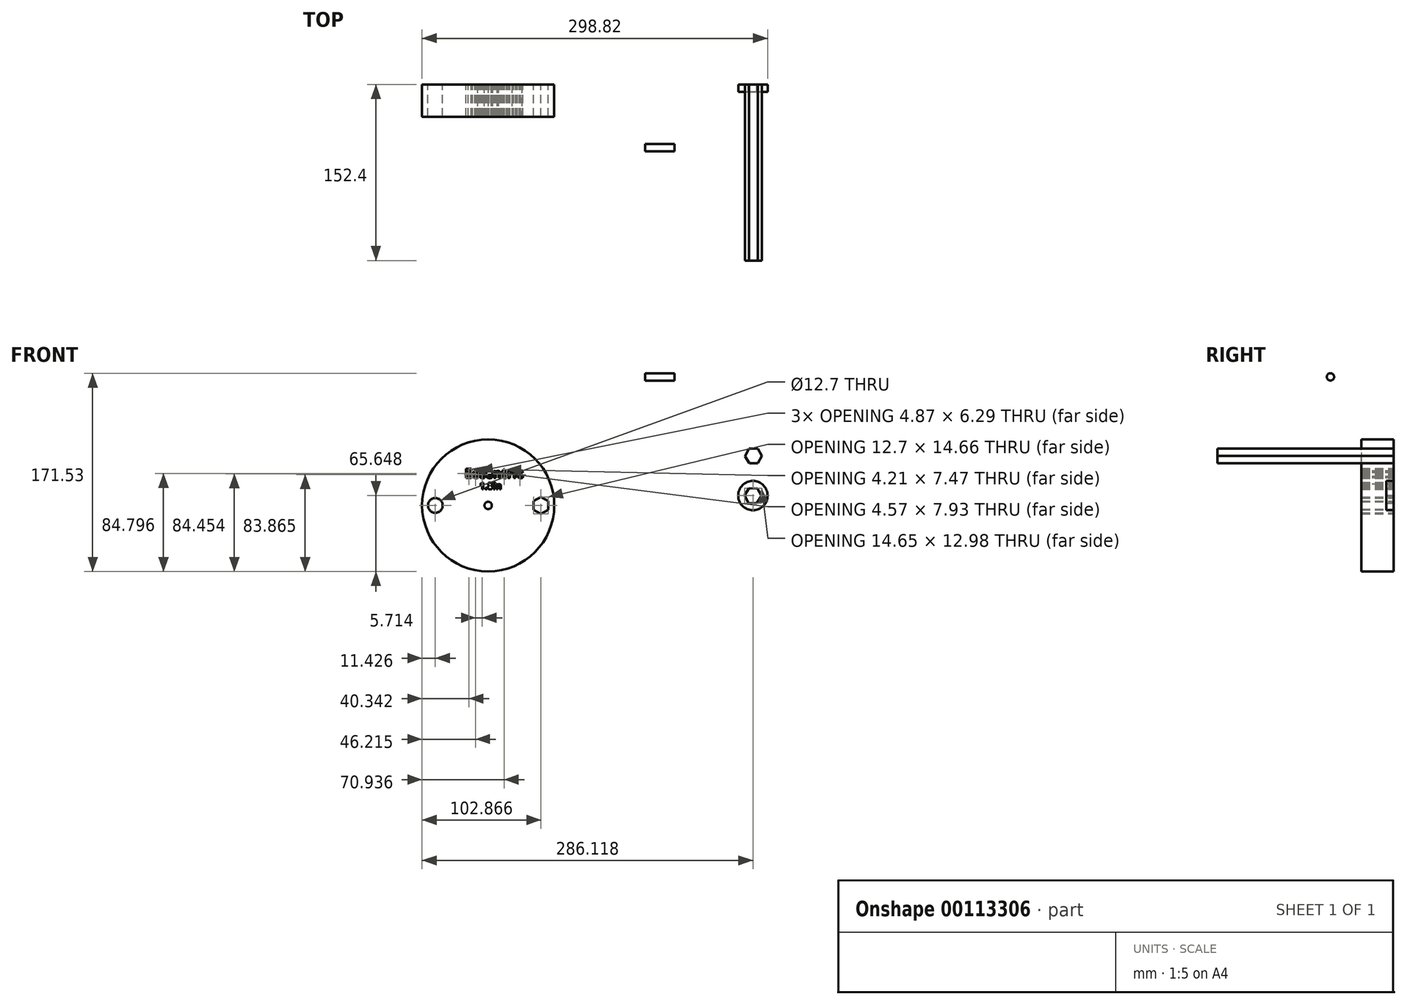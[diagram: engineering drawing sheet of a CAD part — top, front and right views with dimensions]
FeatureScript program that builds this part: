
annotation { "Feature Type Name" : "Feature", "Feature Type Description" : "" }
export const myFeature = defineFeature(function(context is Context, id is Id, definition is map)
    precondition{}
    {
        {
            var Q0;
            Q0=qCreatedBy(makeId("Front.planeOp"),FACE);
            var sketch = newSketch(context, id + "F0", { "sketchPlane" : qUnion([Q0])});
            skCircle(sketch, "E0", {"center": v(0, 0) * mm, "radius": 53.98 * mm});
            skCircle(sketch, "E1", {"center": v(0, 0) * mm, "radius": 45.72 * mm, "construction": true});
            skLineSegment(sketch, "E2", {"start": v(0, 0) * mm, "end": v(45.72, 0) * mm, "construction": true});
            skLineSegment(sketch, "E3", {"start": v(0, 0) * mm, "end": v(-22.86, 39.6) * mm, "construction": true});
            skLineSegment(sketch, "E4", {"start": v(0, 0) * mm, "end": v(-22.86, -39.6) * mm, "construction": true});
            skCircle(sketch, "E5", {"center": v(45.72, 0) * mm, "radius": 3.18 * mm});
            skCircle(sketch, "E6", {"center": v(-22.86, 39.6) * mm, "radius": 3.18 * mm});
            skCircle(sketch, "E7", {"center": v(-22.86, -39.6) * mm, "radius": 3.18 * mm});
            skCircle(sketch, "E8", {"center": v(0, 0) * mm, "radius": 3.18 * mm});
            skSolve(sketch);
        }
        {
            var Q0;
            Q0=makeQuery(id+"F0.imprint","IMPRINT",FACE,{"disambiguationData":[TD([[makeQuery(id+"F0.imprint","IMPRINT",EDGE,{"derivedFrom":sQuery(id+"F0.wireOp",EDGE,"E0")}),1.0]])]});
            extrude(context, id + "F1", {"entities" : qUnion([Q0]), "depth" : 3.17 * mm});
        }
        {
            var Q0;
            Q0=qCreatedBy(makeId("Right.planeOp"),FACE);
            var sketch = newSketch(context, id + "F2", { "sketchPlane" : qUnion([Q0])});
            skCircle(sketch, "E9", {"center": v(-54.81, 63.87) * mm, "radius": 3.18 * mm});
            skSolve(sketch);
        }
        {
            var Q0;
            Q0=makeQuery(id+"F2.imprint","IMPRINT",FACE,{"disambiguationData":[TD([[makeQuery(id+"F2.imprint","IMPRINT",EDGE,{"derivedFrom":sQuery(id+"F2.wireOp",EDGE,"E9")}),1.0]])]});
            extrude(context, id + "F3", {"entities" : qUnion([Q0]), "depth" : 25.4 * mm});
        }
        {
            var Q0;
            Q0=qCreatedBy(makeId("Front.planeOp"),FACE);
            var sketch = newSketch(context, id + "F4", { "sketchPlane" : qUnion([Q0])});
            skCircle(sketch, "E10", {"center": v(-135.8, -47.34) * mm, "radius": 57.15 * mm});
            skCircle(sketch, "E11", {"center": v(-181.51, -47.34) * mm, "radius": 6.35 * mm});
            skText(sketch, "E12", { "text": "Eccentric", "fontName": "OpenSans-Bold.ttf"});
            skCircle(sketch, "E13", {"center": v(-135.8, -47.34) * mm, "radius": 3.18 * mm});
            skText(sketch, "E14", { "text": "1.8in", "fontName": "OpenSans-Bold.ttf"});
            skCircle(sketch, "E15.cCircle", {"center": v(-90.07, -47.34) * mm, "radius": 6.35 * mm, "construction": true});
            skLineSegment(sketch, "E15.0", {"start": v(-83.72, -51) * mm, "end": v(-90.07, -54.67) * mm});
            skLineSegment(sketch, "E15.1", {"start": v(-90.07, -54.67) * mm, "end": v(-96.42, -51) * mm});
            skLineSegment(sketch, "E15.2", {"start": v(-96.42, -51) * mm, "end": v(-96.42, -43.68) * mm});
            skLineSegment(sketch, "E15.3", {"start": v(-96.42, -43.68) * mm, "end": v(-90.07, -40) * mm});
            skLineSegment(sketch, "E15.4", {"start": v(-90.07, -40) * mm, "end": v(-83.72, -43.68) * mm});
            skLineSegment(sketch, "E15.5", {"start": v(-83.72, -43.68) * mm, "end": v(-83.72, -51) * mm});
            skPoint(sketch, "E15.0.midPoint", {"position": v(-86.9, -52.84) * mm});
            const initialGuessF4  = {"E12": [-0.15588, -0.02366, 1, 0, 0.008], "E14": [-0.14326, -0.03332, 1, 0, 0.00577]};
            skSetInitialGuess(sketch, initialGuessF4);
            skSolve(sketch);
        }
        {
            var Q0;
            Q0=makeQuery(id+"F4.imprint","IMPRINT",FACE,{"disambiguationData":[TD([[makeQuery(id+"F4.imprint","IMPRINT",EDGE,{"derivedFrom":sQuery(id+"F4.wireOp",EDGE,"E10")}),1.0]])]});
            extrude(context, id + "F5", {"entities" : qUnion([Q0]), "depth" : 27.94 * mm});
        }
        {
            var Q0;
            Q0=qCreatedBy(makeId("Front.planeOp"),FACE);
            var sketch = newSketch(context, id + "F6", { "sketchPlane" : qUnion([Q0])});
            skCircle(sketch, "E16.cCircle", {"center": v(93.67, -4.58) * mm, "radius": 6.35 * mm, "construction": true});
            skLineSegment(sketch, "E16.0", {"start": v(101, -4.52) * mm, "end": v(97.39, -10.9) * mm});
            skLineSegment(sketch, "E16.1", {"start": v(97.39, -10.9) * mm, "end": v(90.06, -10.96) * mm});
            skLineSegment(sketch, "E16.2", {"start": v(90.06, -10.96) * mm, "end": v(86.33, -4.65) * mm});
            skLineSegment(sketch, "E16.3", {"start": v(86.33, -4.65) * mm, "end": v(89.94, 1.74) * mm});
            skLineSegment(sketch, "E16.4", {"start": v(89.94, 1.74) * mm, "end": v(97.28, 1.8) * mm});
            skLineSegment(sketch, "E16.5", {"start": v(97.28, 1.8) * mm, "end": v(101, -4.52) * mm});
            skPoint(sketch, "E16.0.midPoint", {"position": v(99.2, -7.7) * mm});
            skSolve(sketch);
        }
        {
            var Q0;
            Q0=qCreatedBy(makeId("Front.planeOp"),FACE);
            var sketch = newSketch(context, id + "F7", { "sketchPlane" : qUnion([Q0])});
            skCircle(sketch, "E17.cCircle", {"center": v(93.18, -38.84) * mm, "radius": 6.35 * mm, "construction": true});
            skLineSegment(sketch, "E17.0", {"start": v(100.5, -39.13) * mm, "end": v(96.6, -45.33) * mm});
            skLineSegment(sketch, "E17.1", {"start": v(96.6, -45.33) * mm, "end": v(89.27, -45.04) * mm});
            skLineSegment(sketch, "E17.2", {"start": v(89.27, -45.04) * mm, "end": v(85.85, -38.55) * mm});
            skLineSegment(sketch, "E17.3", {"start": v(85.85, -38.55) * mm, "end": v(89.76, -32.35) * mm});
            skLineSegment(sketch, "E17.4", {"start": v(89.76, -32.35) * mm, "end": v(97.1, -32.64) * mm});
            skLineSegment(sketch, "E17.5", {"start": v(97.1, -32.64) * mm, "end": v(100.5, -39.13) * mm});
            skPoint(sketch, "E17.0.midPoint", {"position": v(98.55, -42.23) * mm});
            skCircle(sketch, "E18", {"center": v(93.18, -38.84) * mm, "radius": 12.7 * mm});
            skSolve(sketch);
        }
        {
            var Q0;
            Q0=makeQuery(id+"F6.imprint","IMPRINT",FACE,{"disambiguationData":[TD([[makeQuery(id+"F6.imprint","IMPRINT",EDGE,{"derivedFrom":sQuery(id+"F6.wireOp",EDGE,"E16.0")}),-1.0]])]});
            extrude(context, id + "F8", {"entities" : qUnion([Q0]), "depth" : 152.4 * mm});
        }
        {
            var Q0;
            Q0=makeQuery(id+"F7.imprint","IMPRINT",FACE,{"disambiguationData":[TD([[makeQuery(id+"F7.imprint","IMPRINT",EDGE,{"derivedFrom":sQuery(id+"F7.wireOp",EDGE,"E17.0")}),1.0]])]});
            extrude(context, id + "F9", {"entities" : qUnion([Q0]), "depth" : 6.35 * mm});
        }
        {
            var Q0;
            Q0=makeQuery(id+"F1.opExtrude","SWEPT_BODY",BODY,{"disambiguationData":[OSD([sQuery(id+"F0.wireOp",EDGE,"E0"),sQuery(id+"F0.wireOp",EDGE,"E5"),sQuery(id+"F0.wireOp",EDGE,"E6"),sQuery(id+"F0.wireOp",EDGE,"E7"),sQuery(id+"F0.wireOp",EDGE,"E8")])]});
            deleteBodies(context, id + "F10", {"entities" : qUnion([Q0])});
        }
    });
